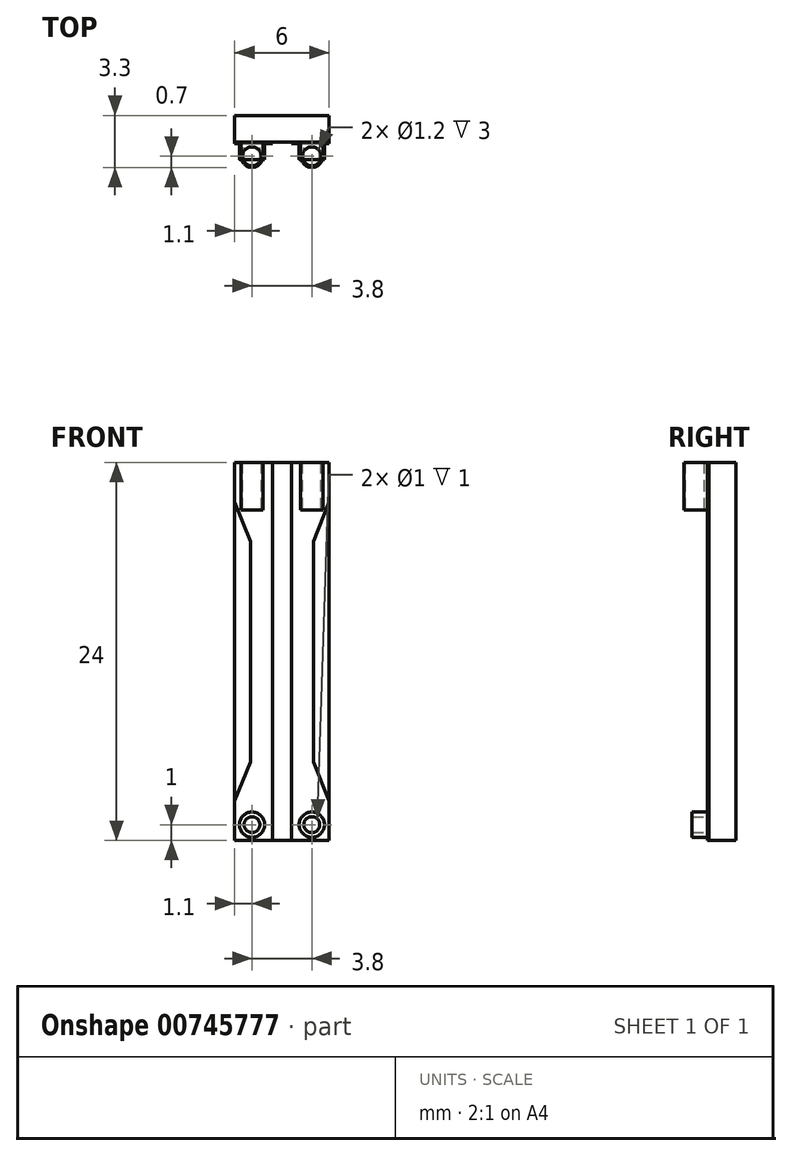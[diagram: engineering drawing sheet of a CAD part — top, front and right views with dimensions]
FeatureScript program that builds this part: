
annotation { "Feature Type Name" : "Feature", "Feature Type Description" : "" }
export const myFeature = defineFeature(function(context is Context, id is Id, definition is map)
    precondition{}
    {
        {
            var Q0;
            Q0=qCreatedBy(makeId("Front.planeOp"),FACE);
            var sketch = newSketch(context, id + "F0", { "sketchPlane" : qUnion([Q0])});
            skLineSegment(sketch, "E0.bottom", {"start": v(-3, 19) * mm, "end": v(3, 19) * mm});
            skLineSegment(sketch, "E0.top", {"start": v(-3, -5) * mm, "end": v(3, -5) * mm});
            skLineSegment(sketch, "E0.left", {"start": v(-3, 19) * mm, "end": v(-3, -5) * mm});
            skLineSegment(sketch, "E0.right", {"start": v(3, 19) * mm, "end": v(3, -5) * mm});
            skSolve(sketch);
        }
        {
            var Q0;
            Q0 = qSketchRegion(id + "F0", true);
            extrude(context, id + "F1", {"entities" : qUnion([Q0]), "depth" : 1.7 * mm, "offsetDistance" : 25 * mm});
        }
        {
            var Q0;
            Q0=makeQuery(id+"F1.opExtrude","CAP_FACE",FACE,{"disambiguationData":[OSD([sQuery(id+"F0.wireOp",EDGE,"E0.bottom"),sQuery(id+"F0.wireOp",EDGE,"E0.top"),sQuery(id+"F0.wireOp",EDGE,"E0.left"),sQuery(id+"F0.wireOp",EDGE,"E0.right")])],"isStart":false});
            var sketch = newSketch(context, id + "F2", { "sketchPlane" : qUnion([Q0])});
            skLineSegment(sketch, "E1", {"start": v(-3, -5) * mm, "end": v(-3, -2.5) * mm});
            skLineSegment(sketch, "E2", {"start": v(-3, -2.5) * mm, "end": v(-2, 0) * mm});
            skLineSegment(sketch, "E3", {"start": v(-2, 0) * mm, "end": v(-2, 7) * mm});
            skLineSegment(sketch, "E4", {"start": v(0, 0) * mm, "end": v(0, 5.6) * mm, "construction": true});
            skLineSegment(sketch, "E5", {"start": v(-3, -5) * mm, "end": v(-0.6, -5) * mm});
            skLineSegment(sketch, "E6", {"start": v(-0.6, -5) * mm, "end": v(-0.6, 7) * mm});
            skLineSegment(sketch, "E7", {"start": v(-3, 7) * mm, "end": v(3, 7) * mm, "construction": true});
            skLineSegment(sketch, "E8.MirrorCS", {"start": v(-0.6, 19) * mm, "end": v(-0.6, 7) * mm});
            skLineSegment(sketch, "E9.MirrorCS", {"start": v(-2, 14) * mm, "end": v(-2, 7) * mm});
            skLineSegment(sketch, "E10.MirrorCS", {"start": v(-3, 16.5) * mm, "end": v(-2, 14) * mm});
            skLineSegment(sketch, "E11.MirrorCS", {"start": v(-3, 19) * mm, "end": v(-3, 16.5) * mm});
            skLineSegment(sketch, "E12.MirrorCS", {"start": v(-3, 19) * mm, "end": v(-0.6, 19) * mm});
            skLineSegment(sketch, "E13.MirrorCS", {"start": v(0.6, -5) * mm, "end": v(0.6, 7) * mm});
            skLineSegment(sketch, "E14.MirrorCS", {"start": v(0.6, 19) * mm, "end": v(0.6, 7) * mm});
            skLineSegment(sketch, "E15.MirrorCS", {"start": v(2, 14) * mm, "end": v(2, 7) * mm});
            skLineSegment(sketch, "E16.MirrorCS", {"start": v(3, 16.5) * mm, "end": v(2, 14) * mm});
            skLineSegment(sketch, "E17.MirrorCS", {"start": v(3, 19) * mm, "end": v(3, 16.5) * mm});
            skLineSegment(sketch, "E18.MirrorCS", {"start": v(3, 19) * mm, "end": v(0.6, 19) * mm});
            skLineSegment(sketch, "E19.MirrorCS", {"start": v(2, 0) * mm, "end": v(2, 7) * mm});
            skLineSegment(sketch, "E20.MirrorCS", {"start": v(3, -2.5) * mm, "end": v(2, 0) * mm});
            skLineSegment(sketch, "E21.MirrorCS", {"start": v(3, -5) * mm, "end": v(3, -2.5) * mm});
            skLineSegment(sketch, "E22.MirrorCS", {"start": v(3, -5) * mm, "end": v(0.6, -5) * mm});
            skSolve(sketch);
        }
        {
            var Q0;
            Q0 = qSketchRegion(id + "F2", true);
            extrude(context, id + "F3", {"entities" : qUnion([Q0]), "depth" : 0.1 * mm, "offsetDistance" : 25 * mm});
        }
        {
            var Q0;
            Q0=makeQuery(id+"F3.opExtrude","CAP_FACE",FACE,{"disambiguationData":[OSD([sQuery(id+"F2.wireOp",EDGE,"E1"),sQuery(id+"F2.wireOp",EDGE,"E2"),sQuery(id+"F2.wireOp",EDGE,"E3"),sQuery(id+"F2.wireOp",EDGE,"E5"),sQuery(id+"F2.wireOp",EDGE,"E6"),sQuery(id+"F2.wireOp",EDGE,"E8.MirrorCS"),sQuery(id+"F2.wireOp",EDGE,"E9.MirrorCS"),sQuery(id+"F2.wireOp",EDGE,"E10.MirrorCS"),sQuery(id+"F2.wireOp",EDGE,"E11.MirrorCS"),sQuery(id+"F2.wireOp",EDGE,"E12.MirrorCS")])],"isStart":false});
            var sketch = newSketch(context, id + "F4", { "sketchPlane" : qUnion([Q0])});
            skCircle(sketch, "E23", {"center": v(-1.9, -4) * mm, "radius": 0.5 * mm});
            skCircle(sketch, "E24", {"center": v(-1.9, -4) * mm, "radius": 0.8 * mm});
            skSolve(sketch);
        }
        {
            var Q0;
            Q0 = qSketchRegion(id + "F4", true);
            extrude(context, id + "F5", {"entities" : qUnion([Q0]), "operationType" : NewBodyOperationType.ADD, "depth" : 1 * mm, "offsetDistance" : 25 * mm});
        }
        {
            var Q0;
            Q0=makeQuery(id+"F3.opExtrude","CAP_FACE",FACE,{"disambiguationData":[OSD([sQuery(id+"F2.wireOp",EDGE,"E14.MirrorCS"),sQuery(id+"F2.wireOp",EDGE,"E15.MirrorCS"),sQuery(id+"F2.wireOp",EDGE,"E16.MirrorCS"),sQuery(id+"F2.wireOp",EDGE,"E17.MirrorCS"),sQuery(id+"F2.wireOp",EDGE,"E18.MirrorCS"),sQuery(id+"F2.wireOp",EDGE,"E19.MirrorCS"),sQuery(id+"F2.wireOp",EDGE,"E20.MirrorCS"),sQuery(id+"F2.wireOp",EDGE,"E21.MirrorCS"),sQuery(id+"F2.wireOp",EDGE,"E22.MirrorCS"),sQuery(id+"F2.wireOp",EDGE,"E13.MirrorCS")])],"isStart":false});
            var sketch = newSketch(context, id + "F6", { "sketchPlane" : qUnion([Q0])});
            skCircle(sketch, "E25", {"center": v(1.9, -4) * mm, "radius": 0.8 * mm});
            skCircle(sketch, "E26", {"center": v(1.9, -4) * mm, "radius": 0.5 * mm});
            skSolve(sketch);
        }
        {
            var Q0;
            Q0 = qSketchRegion(id + "F6", true);
            extrude(context, id + "F7", {"entities" : qUnion([Q0]), "operationType" : NewBodyOperationType.ADD, "depth" : 1 * mm, "offsetDistance" : 25 * mm});
        }
        {
            var Q0;
            Q0=makeQuery(id+"F3.opExtrude","SWEPT_FACE",FACE,{"disambiguationData":[OSD([sQuery(id+"F2.wireOp",EDGE,"E12.MirrorCS")])]});
            var sketch = newSketch(context, id + "F8", { "sketchPlane" : qUnion([Q0])});
            skCircle(sketch, "E27", {"center": v(-1.9, -2.6) * mm, "radius": 0.6 * mm});
            skArc(sketch, "E28", {"start": v(-2.6, -2.6) * mm, "mid": v(-1.9, -3.3) * mm, "end": v(-1.2, -2.6) * mm});
            skLineSegment(sketch, "E29", {"start": v(-1.2, -2.6) * mm, "end": v(-1.2, -1.8) * mm});
            skLineSegment(sketch, "E30", {"start": v(-2.6, -2.6) * mm, "end": v(-2.6, -1.8) * mm});
            skArc(sketch, "E31.1.0.0", {"start": v(1.2, -2.6) * mm, "mid": v(1.9, -3.3) * mm, "end": v(2.6, -2.6) * mm});
            skCircle(sketch, "E31.1.0.1", {"center": v(1.9, -2.6) * mm, "radius": 0.6 * mm});
            skLineSegment(sketch, "E31.1.0.2", {"start": v(1.2, -2.6) * mm, "end": v(1.2, -1.8) * mm});
            skLineSegment(sketch, "E31.1.0.3", {"start": v(2.6, -2.6) * mm, "end": v(2.6, -1.8) * mm});
            skLineSegment(sketch, "E31.direction1", {"start": v(-2.6, -2.6) * mm, "end": v(1.2, -2.6) * mm, "construction": true});
            skLineSegment(sketch, "E32", {"start": v(1.2, -1.8) * mm, "end": v(2.6, -1.8) * mm});
            skSolve(sketch);
        }
        {
            var Q0;
            Q0=makeQuery(id+"F8.imprint","IMPRINT",FACE,{"disambiguationData":[TD([[makeQuery(id+"F8.imprint","IMPRINT",EDGE,{"derivedFrom":sQuery(id+"F8.wireOp",EDGE,"E27")}),-1.0]])]});
            var Q1;
            Q1=makeQuery(id+"F8.imprint","IMPRINT",FACE,{"disambiguationData":[TD([[makeQuery(id+"F8.imprint","IMPRINT",EDGE,{"derivedFrom":sQuery(id+"F8.wireOp",EDGE,"E31.1.0.0")}),1.0]])]});
            extrude(context, id + "F9", {"entities" : qUnion([Q0, Q1]), "operationType" : NewBodyOperationType.ADD, "oppositeDirection" : true, "depth" : 3 * mm, "offsetDistance" : 25 * mm});
        }
    });
